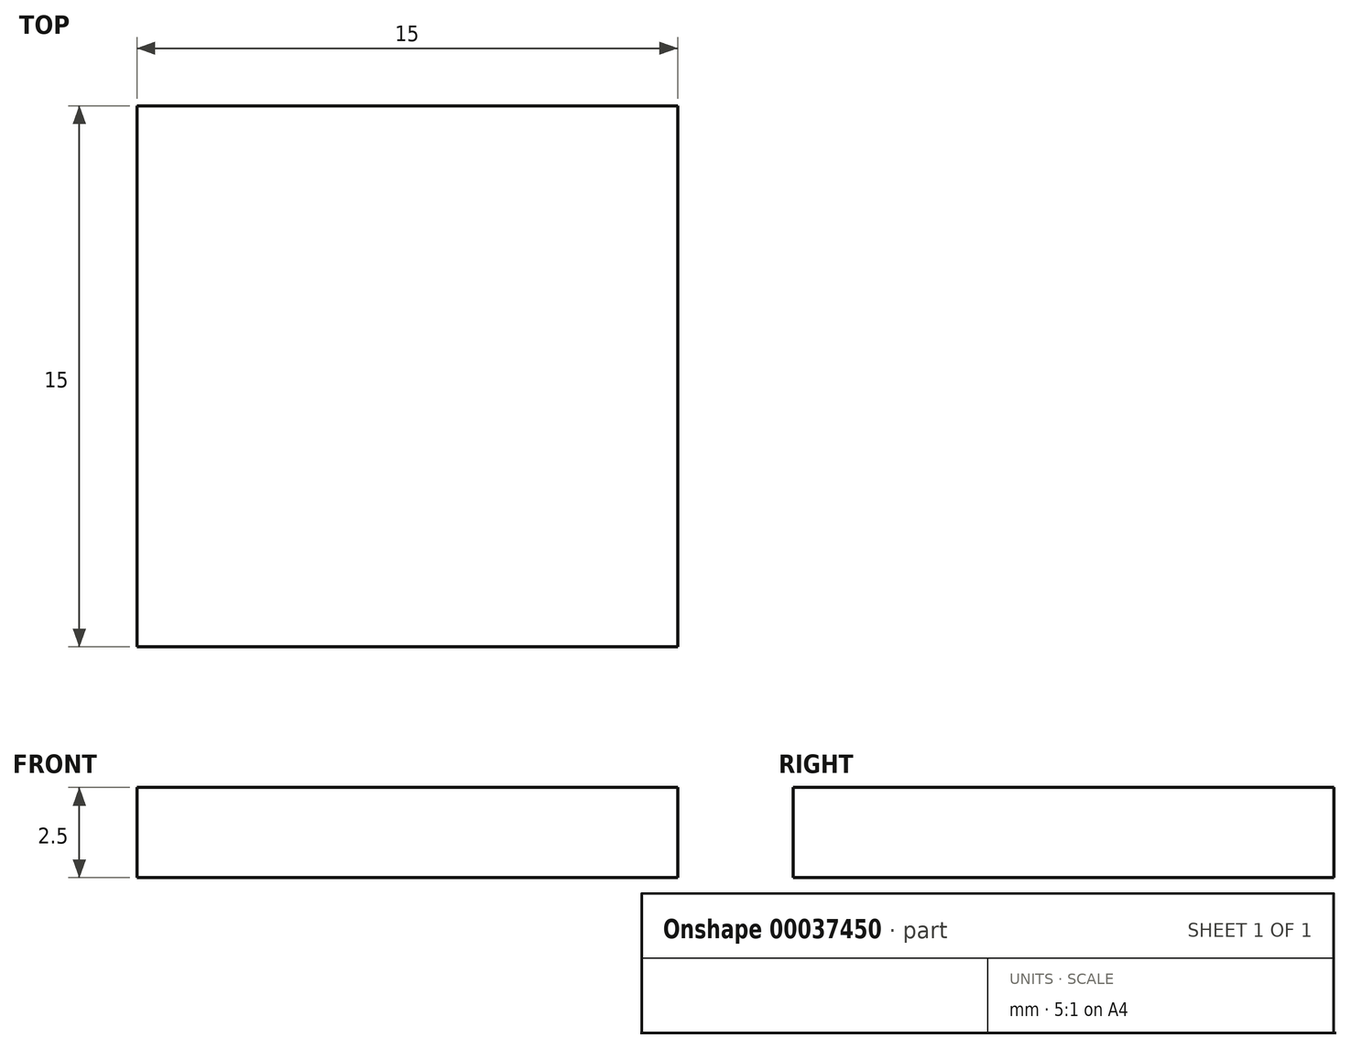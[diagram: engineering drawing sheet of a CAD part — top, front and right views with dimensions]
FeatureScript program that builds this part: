
annotation { "Feature Type Name" : "Feature", "Feature Type Description" : "" }
export const myFeature = defineFeature(function(context is Context, id is Id, definition is map)
    precondition{}
    {
        {
            var Q0;
            Q0=qCreatedBy(makeId("Top.planeOp"),FACE);
            var sketch = newSketch(context, id + "F0", { "sketchPlane" : qUnion([Q0])});
            skLineSegment(sketch, "E0.bottom", {"start": v(0, 0) * mm, "end": v(15, 0) * mm});
            skLineSegment(sketch, "E0.top", {"start": v(0, 15) * mm, "end": v(15, 15) * mm});
            skLineSegment(sketch, "E0.left", {"start": v(0, 0) * mm, "end": v(0, 15) * mm});
            skLineSegment(sketch, "E0.right", {"start": v(15, 0) * mm, "end": v(15, 15) * mm});
            skSolve(sketch);
        }
        {
            var Q0;
            Q0 = qSketchRegion(id + "F0", true);
            extrude(context, id + "F1", {"entities" : qUnion([Q0]), "depth" : 2.5 * mm});
        }
    });
